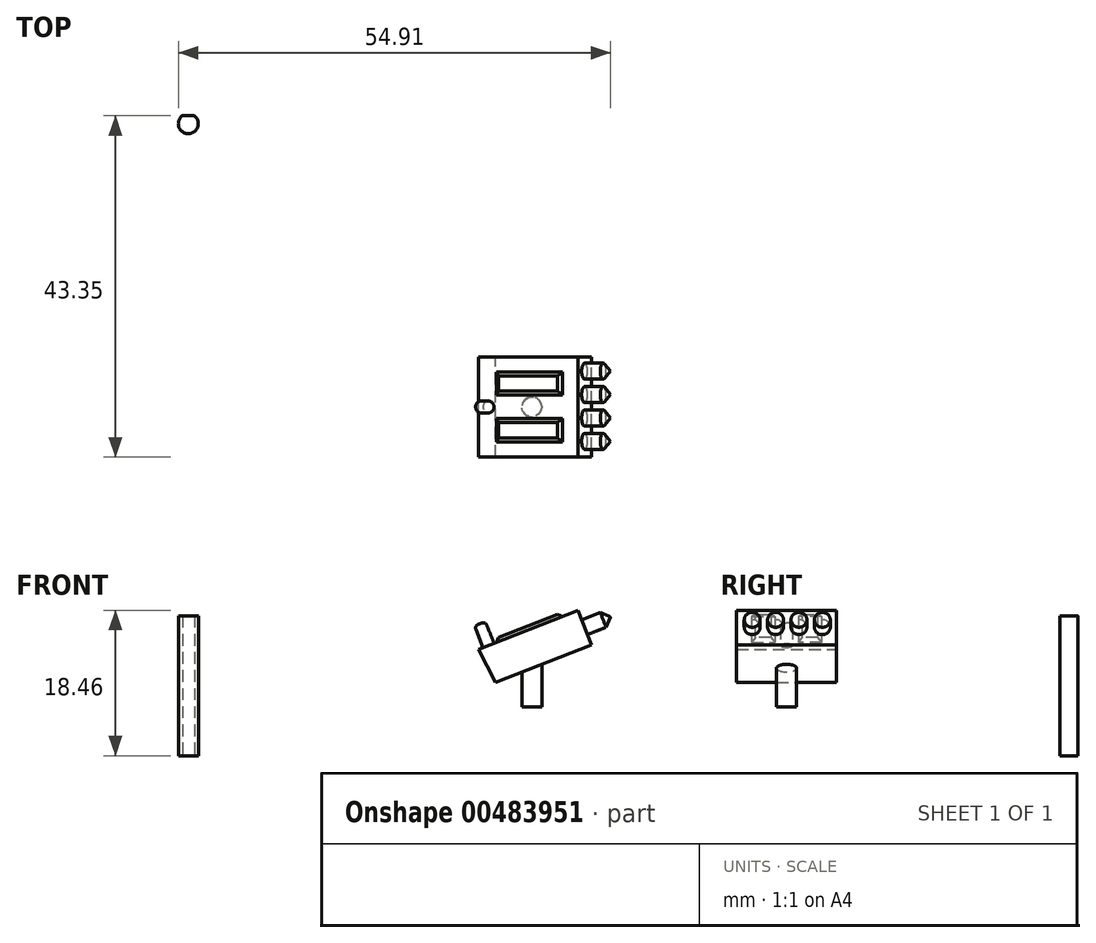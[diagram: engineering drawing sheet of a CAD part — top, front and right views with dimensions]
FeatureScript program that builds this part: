
annotation { "Feature Type Name" : "Feature", "Feature Type Description" : "" }
export const myFeature = defineFeature(function(context is Context, id is Id, definition is map)
    precondition{}
    {
        {
            var Q0;
            Q0=qCreatedBy(makeId("Front.planeOp"),FACE);
            var sketch = newSketch(context, id + "F0", { "sketchPlane" : qUnion([Q0])});
            skLineSegment(sketch, "E0", {"start": v(-5.51, 8.4) * mm, "end": v(7.14, 13.38) * mm});
            skLineSegment(sketch, "E1", {"start": v(7.14, 13.38) * mm, "end": v(8.85, 9.02) * mm});
            skLineSegment(sketch, "E2", {"start": v(8.85, 9.02) * mm, "end": v(-3.34, 4.24) * mm});
            skLineSegment(sketch, "E3", {"start": v(-3.34, 4.24) * mm, "end": v(-5.51, 8.4) * mm});
            skLineSegment(sketch, "E4", {"start": v(1.27, 6.05) * mm, "end": v(1.27, 1.16) * mm});
            skLineSegment(sketch, "E5", {"start": v(1.27, 1.16) * mm, "end": v(0, 1.16) * mm});
            skLineSegment(sketch, "E6", {"start": v(0, 1.16) * mm, "end": v(0, 5.55) * mm});
            skLineSegment(sketch, "E7", {"start": v(1.27, 1.16) * mm, "end": v(2.54, 1.16) * mm});
            skLineSegment(sketch, "E8", {"start": v(2.54, 1.16) * mm, "end": v(2.54, 6.55) * mm});
            skLineSegment(sketch, "E9", {"start": v(2.54, 6.55) * mm, "end": v(1.27, 6.05) * mm});
            skSolve(sketch);
        }
        {
            var Q0;
            Q0=makeQuery(id+"F0.imprint","IMPRINT",FACE,{"disambiguationData":[TD([[makeQuery(id+"F0.imprint","IMPRINT",EDGE,{"derivedFrom":sQuery(id+"F0.wireOp",EDGE,"E4")}),1.0]])]});
            var Q1;
            Q1=sQuery(id+"F0.wireOp",EDGE,"E4");
            revolve(context, id + "F1", {"entities" : qUnion([Q0]), "axis" : qUnion([Q1]), "revolveType" : RevolveType.FULL});
        }
        {
            var Q0;
            Q0=makeQuery(id+"F0.imprint","IMPRINT",FACE,{"disambiguationData":[TD([[makeQuery(id+"F0.imprint","IMPRINT",EDGE,{"derivedFrom":sQuery(id+"F0.wireOp",EDGE,"E0")}),-1.0]])]});
            extrude(context, id + "F2", {"entities" : qUnion([Q0]), "operationType" : NewBodyOperationType.ADD, "endBound" : BoundingType.SYMMETRIC, "depth" : 12.7 * mm});
        }
        {
            var Q0;
            Q0=makeQuery(id+"F2.opExtrude","SWEPT_FACE",FACE,{"disambiguationData":[OSD([sQuery(id+"F0.wireOp",EDGE,"E1")])]});
            var sketch = newSketch(context, id + "F3", { "sketchPlane" : qUnion([Q0])});
            skCircle(sketch, "E10", {"center": v(-4.37, 7.57) * mm, "radius": 1.02 * mm});
            skCircle(sketch, "E11.1.0.0", {"center": v(-1.4, 7.57) * mm, "radius": 1.02 * mm});
            skCircle(sketch, "E11.2.0.0", {"center": v(1.57, 7.57) * mm, "radius": 1.02 * mm});
            skCircle(sketch, "E11.3.0.0", {"center": v(4.54, 7.57) * mm, "radius": 1.02 * mm});
            skLineSegment(sketch, "E11.direction1", {"start": v(-4.37, 7.57) * mm, "end": v(-1.4, 7.57) * mm, "construction": true});
            skSolve(sketch);
        }
        {
            var Q0;
            Q0=makeQuery(id+"F3.imprint","IMPRINT",FACE,{"disambiguationData":[TD([[makeQuery(id+"F3.imprint","IMPRINT",EDGE,{"derivedFrom":sQuery(id+"F3.wireOp",EDGE,"E10")}),1.0]])]});
            var Q1;
            Q1=makeQuery(id+"F3.imprint","IMPRINT",FACE,{"disambiguationData":[TD([[makeQuery(id+"F3.imprint","IMPRINT",EDGE,{"derivedFrom":sQuery(id+"F3.wireOp",EDGE,"E11.2.0.0")}),1.0]])]});
            var Q2;
            Q2=makeQuery(id+"F3.imprint","IMPRINT",FACE,{"disambiguationData":[TD([[makeQuery(id+"F3.imprint","IMPRINT",EDGE,{"derivedFrom":sQuery(id+"F3.wireOp",EDGE,"E11.3.0.0")}),1.0]])]});
            var Q3;
            Q3=makeQuery(id+"F3.imprint","IMPRINT",FACE,{"disambiguationData":[TD([[makeQuery(id+"F3.imprint","IMPRINT",EDGE,{"derivedFrom":sQuery(id+"F3.wireOp",EDGE,"E11.1.0.0")}),1.0]])]});
            extrude(context, id + "F4", {"entities" : qUnion([Q0, Q1, Q2, Q3]), "operationType" : NewBodyOperationType.ADD, "depth" : 3.56 * mm});
        }
        {
            var Q0;
            Q0=makeQuery(id+"F4.opExtrude","CAP_EDGE",EDGE,{"disambiguationData":[OSD([sQuery(id+"F3.wireOp",EDGE,"E10")])],"isStart":false});
            var Q1;
            Q1=makeQuery(id+"F4.opExtrude","CAP_EDGE",EDGE,{"disambiguationData":[OSD([sQuery(id+"F3.wireOp",EDGE,"E11.1.0.0")])],"isStart":false});
            var Q2;
            Q2=makeQuery(id+"F4.opExtrude","CAP_EDGE",EDGE,{"disambiguationData":[OSD([sQuery(id+"F3.wireOp",EDGE,"E11.2.0.0")])],"isStart":false});
            var Q3;
            Q3=makeQuery(id+"F4.opExtrude","CAP_EDGE",EDGE,{"disambiguationData":[OSD([sQuery(id+"F3.wireOp",EDGE,"E11.3.0.0")])],"isStart":false});
            chamfer(context, id + "F5", {"entities" : qUnion([Q0, Q1, Q2, Q3]), "width" : 1.02 * mm, "tangentPropagation" : true});
        }
        {
            var Q0;
            Q0=makeQuery(id+"F2.opExtrude","SWEPT_FACE",FACE,{"disambiguationData":[OSD([sQuery(id+"F0.wireOp",EDGE,"E0")])]});
            var sketch = newSketch(context, id + "F6", { "sketchPlane" : qUnion([Q0])});
            skLineSegment(sketch, "E12.bottom", {"start": v(9.43, 4.46) * mm, "end": v(0.4, 4.46) * mm});
            skLineSegment(sketch, "E12.top", {"start": v(9.43, 1.5) * mm, "end": v(0.4, 1.5) * mm});
            skLineSegment(sketch, "E12.left", {"start": v(9.43, 4.46) * mm, "end": v(9.43, 1.5) * mm});
            skLineSegment(sketch, "E12.right", {"start": v(0.4, 4.46) * mm, "end": v(0.4, 1.5) * mm});
            skLineSegment(sketch, "E13.MirrorCS", {"start": v(9.43, -1.5) * mm, "end": v(0.4, -1.5) * mm});
            skLineSegment(sketch, "E14.MirrorCS", {"start": v(9.43, -4.46) * mm, "end": v(9.43, -1.5) * mm});
            skLineSegment(sketch, "E15.MirrorCS", {"start": v(9.43, -4.46) * mm, "end": v(0.4, -4.46) * mm});
            skLineSegment(sketch, "E16.MirrorCS", {"start": v(0.4, -4.46) * mm, "end": v(0.4, -1.5) * mm});
            skCircle(sketch, "E17", {"center": v(-0.68, 0) * mm, "radius": 0.75 * mm});
            skSolve(sketch);
        }
        {
            var Q0;
            Q0=makeQuery(id+"F6.imprint","IMPRINT",FACE,{"disambiguationData":[TD([[makeQuery(id+"F6.imprint","IMPRINT",EDGE,{"derivedFrom":sQuery(id+"F6.wireOp",EDGE,"E12.bottom")}),1.0]])]});
            var Q1;
            Q1=makeQuery(id+"F6.imprint","IMPRINT",FACE,{"disambiguationData":[TD([[makeQuery(id+"F6.imprint","IMPRINT",EDGE,{"derivedFrom":sQuery(id+"F6.wireOp",EDGE,"E13.MirrorCS")}),1.0]])]});
            extrude(context, id + "F7", {"entities" : qUnion([Q0, Q1]), "operationType" : NewBodyOperationType.ADD, "depth" : 0.5 * mm});
        }
        {
            var Q0;
            Q0=makeQuery(id+"F7.opExtrude","CAP_FACE",FACE,{"disambiguationData":[OSD([sQuery(id+"F6.wireOp",EDGE,"E12.bottom"),sQuery(id+"F6.wireOp",EDGE,"E12.top"),sQuery(id+"F6.wireOp",EDGE,"E12.left"),sQuery(id+"F6.wireOp",EDGE,"E12.right")])],"isStart":false});
            var Q1;
            Q1=makeQuery(id+"F7.opExtrude","CAP_FACE",FACE,{"disambiguationData":[OSD([sQuery(id+"F6.wireOp",EDGE,"E13.MirrorCS"),sQuery(id+"F6.wireOp",EDGE,"E14.MirrorCS"),sQuery(id+"F6.wireOp",EDGE,"E15.MirrorCS"),sQuery(id+"F6.wireOp",EDGE,"E16.MirrorCS")])],"isStart":false});
            chamfer(context, id + "F8", {"entities" : qUnion([Q0, Q1]), "width" : 0.5 * mm, "tangentPropagation" : true});
        }
        {
            var Q0;
            Q0=makeQuery(id+"F6.imprint","IMPRINT",FACE,{"disambiguationData":[TD([[makeQuery(id+"F6.imprint","IMPRINT",EDGE,{"derivedFrom":sQuery(id+"F6.wireOp",EDGE,"E17")}),1.0]])]});
            extrude(context, id + "F9", {"entities" : qUnion([Q0]), "operationType" : NewBodyOperationType.ADD, "depth" : 3 * mm});
        }
        {
            var Q0;
            Q0=makeQuery(id+"F9.opExtrude","CAP_FACE",FACE,{"disambiguationData":[OSD([sQuery(id+"F6.wireOp",EDGE,"E17")])],"isStart":false});
            fillet(context, id + "F10", {"entities" : qUnion([Q0]), "radius" : 0.5 * mm, "tangentPropagation" : true, "allowEdgeOverflow" : false});
        }
        {
            var Q0;
            Q0=qCreatedBy(makeId("Top.planeOp"),FACE);
            var sketch = newSketch(context, id + "F11", { "sketchPlane" : qUnion([Q0])});
            skFitSpline(sketch, "E18", {"points": [v(-57.76, 39.9) * mm, v(-25.97, 39.9) * mm], "startDerivative": vector(23.49, -11.18) * mm, "endDerivative": vector(25.43, 12.15) * mm});
            skFitSpline(sketch, "E19.0", {"points": [v(-58.63, 38.07) * mm, v(-57.54, 37.55) * mm, v(-55.15, 36.66) * mm, v(-49.75, 35.38) * mm, v(-42.14, 34.7) * mm, v(-34.42, 35.28) * mm, v(-28.8, 36.57) * mm, v(-26.26, 37.51) * mm, v(-25.09, 38.07) * mm]});
            skLineSegment(sketch, "E20", {"start": v(-25.97, 39.9) * mm, "end": v(-25.97, 37.68) * mm});
            skLineSegment(sketch, "E21", {"start": v(-57.76, 39.9) * mm, "end": v(-57.76, 37.68) * mm});
            skCircle(sketch, "E22", {"center": v(-42.36, 35.98) * mm, "radius": 1.27 * mm});
            skSolve(sketch);
        }
        {
            var Q0;
            {var subQ0=sQuery(id+"F11.wireOp",EDGE,"E21");Q0=makeQuery(id+"F11.imprint","IMPRINT",FACE,{"disambiguationData":[TD([[makeQuery(id+"F11.imprint","IMPRINT",EDGE,{"derivedFrom":subQ0}),1.0]])]});}
            var Q1;
            {var subQ0=sQuery(id+"F11.wireOp",EDGE,"E22");var subQ1=sQuery(id+"F11.wireOp",EDGE,"E18");var subQ2=makeQuery(id+"F11.imprint","INTERSECT",VERTEX,{"disambiguationData":[OD(0.0)],"derivedFrom":[subQ1,subQ0]});Q1=makeQuery(id+"F11.imprint","IMPRINT",FACE,{"disambiguationData":[TD([[makeQuery(id+"F11.imprint","IMPRINT",EDGE,{"disambiguationData":[TD([[subQ2,-1.0]])],"derivedFrom":subQ1}),-1.0]])]});}
            var Q2;
            {var subQ0=sQuery(id+"F11.wireOp",EDGE,"E20");Q2=makeQuery(id+"F11.imprint","IMPRINT",FACE,{"disambiguationData":[TD([[makeQuery(id+"F11.imprint","IMPRINT",EDGE,{"derivedFrom":subQ0}),-1.0]])]});}
            extrude(context, id + "F12", {"entities" : qUnion([Q0, Q1, Q2]), "depth" : 12.7 * mm});
        }
        {
            var Q0;
            {var subQ0=sQuery(id+"F11.wireOp",EDGE,"E22");var subQ1=sQuery(id+"F11.wireOp",EDGE,"E18");var subQ2=makeQuery(id+"F11.imprint","INTERSECT",VERTEX,{"disambiguationData":[OD(0.0)],"derivedFrom":[subQ1,subQ0]});Q0=makeQuery(id+"F11.imprint","IMPRINT",FACE,{"disambiguationData":[TD([[makeQuery(id+"F11.imprint","IMPRINT",EDGE,{"disambiguationData":[TD([[subQ2,-1.0]])],"derivedFrom":subQ1}),-1.0]])]});}
            extrude(context, id + "F13", {"entities" : qUnion([Q0]), "operationType" : NewBodyOperationType.ADD, "oppositeDirection" : true, "depth" : 5.08 * mm});
        }
    });
